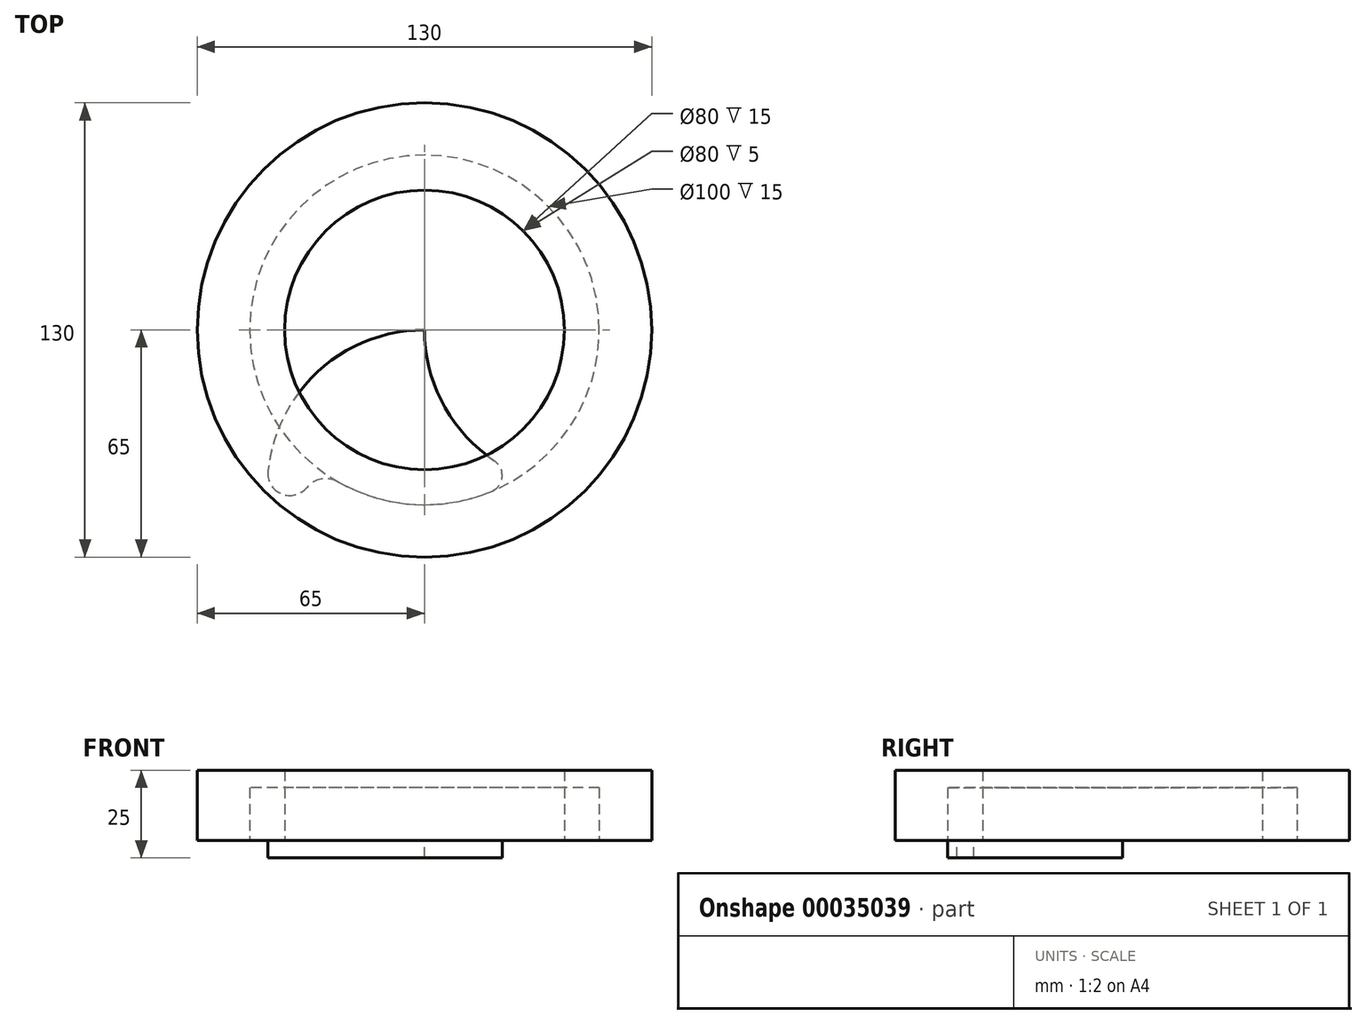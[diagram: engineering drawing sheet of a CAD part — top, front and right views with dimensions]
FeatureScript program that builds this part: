
annotation { "Feature Type Name" : "Feature", "Feature Type Description" : "" }
export const myFeature = defineFeature(function(context is Context, id is Id, definition is map)
    precondition{}
    {
        {
            var Q0;
            Q0=qCreatedBy(makeId("Top.planeOp"),FACE);
            var sketch = newSketch(context, id + "F0", { "sketchPlane" : qUnion([Q0])});
            skCircle(sketch, "E0", {"center": v(0, 0) * mm, "radius": 40 * mm});
            skCircle(sketch, "E1", {"center": v(0, 0) * mm, "radius": 50 * mm});
            skCircle(sketch, "E2", {"center": v(0, 0) * mm, "radius": 65 * mm});
            skLineSegment(sketch, "E3", {"start": v(50, 0) * mm, "end": v(40, 0) * mm});
            skPoint(sketch, "E4", {"position": v(45, 0) * mm});
            skCircle(sketch, "E5", {"center": v(45, 0) * mm, "radius": 45 * mm});
            skLineSegment(sketch, "E6", {"start": v(0, -40) * mm, "end": v(0, -50) * mm});
            skPoint(sketch, "E7", {"position": v(0, -45) * mm});
            skCircle(sketch, "E8", {"center": v(0, -45) * mm, "radius": 45 * mm});
            skCircle(sketch, "E9", {"center": v(-38.5, -41.07) * mm, "radius": 6.3 * mm});
            skArc(sketch, "E10", {"start": v(-24.73, -43.45) * mm, "mid": v(-29.5, -42.64) * mm, "end": v(-33.66, -45.08) * mm});
            skSolve(sketch);
        }
        {
            var Q0;
            {var subQ1=sQuery(id+"F0.wireOp",EDGE,"E1");var subQ5=sQuery(id+"F0.wireOp",EDGE,"E5");var subQ7=makeQuery(id+"F0.imprint","INTERSECT",VERTEX,{"disambiguationData":[OD(0.0)],"derivedFrom":[subQ1,subQ5]});Q0=makeQuery(id+"F0.imprint","IMPRINT",FACE,{"disambiguationData":[TD([[makeQuery(id+"F0.imprint","IMPRINT",EDGE,{"disambiguationData":[TD([[subQ7,-1.0]])],"derivedFrom":subQ1}),-1.0]])]});}
            var Q1;
            {var subQ5=sQuery(id+"F0.wireOp",EDGE,"E1");var subQ9=makeQuery(id+"F0.imprint","INTERSECT",VERTEX,{"derivedFrom":[subQ5,sQuery(id+"F0.wireOp",EDGE,"E6")]});Q1=makeQuery(id+"F0.imprint","IMPRINT",FACE,{"disambiguationData":[TD([[makeQuery(id+"F0.imprint","IMPRINT",EDGE,{"disambiguationData":[TD([[subQ9,1.0]])],"derivedFrom":subQ5}),-1.0]])]});}
            var Q2;
            {var subQ3=sQuery(id+"F0.wireOp",EDGE,"E1");var subQ11=makeQuery(id+"F0.imprint","INTERSECT",VERTEX,{"derivedFrom":[subQ3,sQuery(id+"F0.wireOp",EDGE,"E3")]});Q2=makeQuery(id+"F0.imprint","IMPRINT",FACE,{"disambiguationData":[TD([[makeQuery(id+"F0.imprint","IMPRINT",EDGE,{"disambiguationData":[TD([[subQ11,-1.0]])],"derivedFrom":subQ3}),-1.0]])]});}
            var Q3;
            {var subQ1=sQuery(id+"F0.wireOp",EDGE,"E5");var subQ3=sQuery(id+"F0.wireOp",EDGE,"E1");var subQ5=makeQuery(id+"F0.imprint","INTERSECT",VERTEX,{"disambiguationData":[OD(1.0)],"derivedFrom":[subQ3,subQ1]});Q3=makeQuery(id+"F0.imprint","IMPRINT",FACE,{"disambiguationData":[TD([[makeQuery(id+"F0.imprint","IMPRINT",EDGE,{"disambiguationData":[TD([[subQ5,-1.0]])],"derivedFrom":subQ3}),-1.0]])]});}
            var Q4;
            {var subQ0=sQuery(id+"F0.wireOp",EDGE,"94395ed1-b184-4d6a-bdb4-7635c48ce84e");var subQ3=sQuery(id+"F0.wireOp",EDGE,"E1");var subQ4=makeQuery(id+"F0.imprint","INTERSECT",VERTEX,{"derivedFrom":[subQ3,subQ0]});Q4=makeQuery(id+"F0.imprint","IMPRINT",FACE,{"disambiguationData":[TD([[makeQuery(id+"F0.imprint","IMPRINT",EDGE,{"disambiguationData":[TD([[subQ4,-1.0]])],"derivedFrom":subQ3}),-1.0]])]});}
            var Q5;
            {var subQ0=sQuery(id+"F0.wireOp",EDGE,"94395ed1-b184-4d6a-bdb4-7635c48ce84e");var subQ2=makeQuery(id+"F0.imprint","INTERSECT",VERTEX,{"derivedFrom":[sQuery(id+"F0.wireOp",EDGE,"E1"),subQ0]});Q5=makeQuery(id+"F0.imprint","IMPRINT",FACE,{"disambiguationData":[TD([[makeQuery(id+"F0.imprint","IMPRINT",EDGE,{"disambiguationData":[TD([[subQ2,1.0]])],"derivedFrom":subQ0}),1.0]])]});}
            var Q6;
            {var subQ0=sQuery(id+"F0.wireOp",EDGE,"E8");var subQ3=sQuery(id+"F0.wireOp",EDGE,"E2");var subQ4=makeQuery(id+"F0.imprint","INTERSECT",VERTEX,{"disambiguationData":[OD(1.0)],"derivedFrom":[subQ3,subQ0]});Q6=makeQuery(id+"F0.imprint","IMPRINT",FACE,{"disambiguationData":[TD([[makeQuery(id+"F0.imprint","IMPRINT",EDGE,{"disambiguationData":[TD([[subQ4,-1.0]])],"derivedFrom":subQ3}),1.0]])]});}
            var Q7;
            {var subQ3=sQuery(id+"F0.wireOp",EDGE,"E0");var subQ5=sQuery(id+"F0.wireOp",EDGE,"E5");var subQ7=makeQuery(id+"F0.imprint","INTERSECT",VERTEX,{"disambiguationData":[OD(0.0)],"derivedFrom":[subQ3,subQ5]});Q7=makeQuery(id+"F0.imprint","IMPRINT",FACE,{"disambiguationData":[TD([[makeQuery(id+"F0.imprint","IMPRINT",EDGE,{"disambiguationData":[TD([[subQ7,-1.0]])],"derivedFrom":subQ3}),-1.0]])]});}
            var Q8;
            {var subQ5=sQuery(id+"F0.wireOp",EDGE,"E3");Q8=makeQuery(id+"F0.imprint","IMPRINT",FACE,{"disambiguationData":[TD([[makeQuery(id+"F0.imprint","IMPRINT",EDGE,{"derivedFrom":subQ5}),-1.0]])]});}
            var Q9;
            {var subQ5=sQuery(id+"F0.wireOp",EDGE,"E3");Q9=makeQuery(id+"F0.imprint","IMPRINT",FACE,{"disambiguationData":[TD([[makeQuery(id+"F0.imprint","IMPRINT",EDGE,{"derivedFrom":subQ5}),1.0]])]});}
            var Q10;
            {var subQ3=sQuery(id+"F0.wireOp",EDGE,"E0");var subQ5=sQuery(id+"F0.wireOp",EDGE,"E5");var subQ7=makeQuery(id+"F0.imprint","INTERSECT",VERTEX,{"disambiguationData":[OD(1.0)],"derivedFrom":[subQ3,subQ5]});Q10=makeQuery(id+"F0.imprint","IMPRINT",FACE,{"disambiguationData":[TD([[makeQuery(id+"F0.imprint","IMPRINT",EDGE,{"disambiguationData":[TD([[subQ7,-1.0]])],"derivedFrom":subQ3}),-1.0]])]});}
            var Q11;
            {var subQ0=sQuery(id+"F0.wireOp",EDGE,"E6");Q11=makeQuery(id+"F0.imprint","IMPRINT",FACE,{"disambiguationData":[TD([[makeQuery(id+"F0.imprint","IMPRINT",EDGE,{"derivedFrom":subQ0}),1.0]])]});}
            var Q12;
            {var subQ5=sQuery(id+"F0.wireOp",EDGE,"E6");Q12=makeQuery(id+"F0.imprint","IMPRINT",FACE,{"disambiguationData":[TD([[makeQuery(id+"F0.imprint","IMPRINT",EDGE,{"derivedFrom":subQ5}),-1.0]])]});}
            var Q13;
            {var subQ1=sQuery(id+"F0.wireOp",EDGE,"E8");var subQ3=sQuery(id+"F0.wireOp",EDGE,"E1");var subQ5=makeQuery(id+"F0.imprint","INTERSECT",VERTEX,{"disambiguationData":[OD(0.0)],"derivedFrom":[subQ3,subQ1]});Q13=makeQuery(id+"F0.imprint","IMPRINT",FACE,{"disambiguationData":[TD([[makeQuery(id+"F0.imprint","IMPRINT",EDGE,{"disambiguationData":[TD([[subQ5,-1.0]])],"derivedFrom":subQ3}),-1.0]])]});}
            var Q14;
            {var subQ0=sQuery(id+"F0.wireOp",EDGE,"E9");var subQ2=makeQuery(id+"F0.imprint","INTERSECT",VERTEX,{"derivedFrom":[sQuery(id+"F0.wireOp",EDGE,"E1"),subQ0]});Q14=makeQuery(id+"F0.imprint","IMPRINT",FACE,{"disambiguationData":[TD([[makeQuery(id+"F0.imprint","IMPRINT",EDGE,{"disambiguationData":[TD([[subQ2,-1.0]])],"derivedFrom":subQ0}),1.0]])]});}
            var Q15;
            {var subQ0=sQuery(id+"F0.wireOp",EDGE,"E10");Q15=makeQuery(id+"F0.imprint","IMPRINT",FACE,{"disambiguationData":[TD([[makeQuery(id+"F0.imprint","IMPRINT",EDGE,{"derivedFrom":subQ0}),-1.0]])]});}
            extrude(context, id + "F1", {"entities" : qUnion([Q0, Q1, Q2, Q3, Q4, Q5, Q6, Q7, Q8, Q9, Q10, Q11, Q12, Q13, Q14, Q15]), "depth" : 20 * mm});
        }
        {
            var Q0;
            {var subQ5=sQuery(id+"F0.wireOp",EDGE,"E3");Q0=makeQuery(id+"F0.imprint","IMPRINT",FACE,{"disambiguationData":[TD([[makeQuery(id+"F0.imprint","IMPRINT",EDGE,{"derivedFrom":subQ5}),-1.0]])]});}
            var Q1;
            {var subQ5=sQuery(id+"F0.wireOp",EDGE,"E3");Q1=makeQuery(id+"F0.imprint","IMPRINT",FACE,{"disambiguationData":[TD([[makeQuery(id+"F0.imprint","IMPRINT",EDGE,{"derivedFrom":subQ5}),1.0]])]});}
            var Q2;
            {var subQ3=sQuery(id+"F0.wireOp",EDGE,"E0");var subQ5=sQuery(id+"F0.wireOp",EDGE,"E5");var subQ7=makeQuery(id+"F0.imprint","INTERSECT",VERTEX,{"disambiguationData":[OD(1.0)],"derivedFrom":[subQ3,subQ5]});Q2=makeQuery(id+"F0.imprint","IMPRINT",FACE,{"disambiguationData":[TD([[makeQuery(id+"F0.imprint","IMPRINT",EDGE,{"disambiguationData":[TD([[subQ7,-1.0]])],"derivedFrom":subQ3}),-1.0]])]});}
            var Q3;
            {var subQ0=sQuery(id+"F0.wireOp",EDGE,"E6");Q3=makeQuery(id+"F0.imprint","IMPRINT",FACE,{"disambiguationData":[TD([[makeQuery(id+"F0.imprint","IMPRINT",EDGE,{"derivedFrom":subQ0}),1.0]])]});}
            var Q4;
            {var subQ5=sQuery(id+"F0.wireOp",EDGE,"E6");Q4=makeQuery(id+"F0.imprint","IMPRINT",FACE,{"disambiguationData":[TD([[makeQuery(id+"F0.imprint","IMPRINT",EDGE,{"derivedFrom":subQ5}),-1.0]])]});}
            var Q5;
            {var subQ3=sQuery(id+"F0.wireOp",EDGE,"E0");var subQ5=sQuery(id+"F0.wireOp",EDGE,"E5");var subQ7=makeQuery(id+"F0.imprint","INTERSECT",VERTEX,{"disambiguationData":[OD(0.0)],"derivedFrom":[subQ3,subQ5]});Q5=makeQuery(id+"F0.imprint","IMPRINT",FACE,{"disambiguationData":[TD([[makeQuery(id+"F0.imprint","IMPRINT",EDGE,{"disambiguationData":[TD([[subQ7,-1.0]])],"derivedFrom":subQ3}),-1.0]])]});}
            extrude(context, id + "F2", {"entities" : qUnion([Q0, Q1, Q2, Q3, Q4, Q5]), "operationType" : NewBodyOperationType.REMOVE, "depth" : 15 * mm});
        }
        {
            var Q0;
            {var subQ5=sQuery(id+"F0.wireOp",EDGE,"E6");Q0=makeQuery(id+"F0.imprint","IMPRINT",FACE,{"disambiguationData":[TD([[makeQuery(id+"F0.imprint","IMPRINT",EDGE,{"derivedFrom":subQ5}),-1.0]])]});}
            var Q1;
            {var subQ0=sQuery(id+"F0.wireOp",EDGE,"E6");Q1=makeQuery(id+"F0.imprint","IMPRINT",FACE,{"disambiguationData":[TD([[makeQuery(id+"F0.imprint","IMPRINT",EDGE,{"derivedFrom":subQ0}),1.0]])]});}
            var Q2;
            {var subQ3=sQuery(id+"F0.wireOp",EDGE,"E0");var subQ5=sQuery(id+"F0.wireOp",EDGE,"E5");var subQ7=makeQuery(id+"F0.imprint","INTERSECT",VERTEX,{"disambiguationData":[OD(1.0)],"derivedFrom":[subQ3,subQ5]});Q2=makeQuery(id+"F0.imprint","IMPRINT",FACE,{"disambiguationData":[TD([[makeQuery(id+"F0.imprint","IMPRINT",EDGE,{"disambiguationData":[TD([[subQ7,-1.0]])],"derivedFrom":subQ3}),-1.0]])]});}
            var Q3;
            {var subQ5=sQuery(id+"F0.wireOp",EDGE,"E3");Q3=makeQuery(id+"F0.imprint","IMPRINT",FACE,{"disambiguationData":[TD([[makeQuery(id+"F0.imprint","IMPRINT",EDGE,{"derivedFrom":subQ5}),1.0]])]});}
            var Q4;
            {var subQ5=sQuery(id+"F0.wireOp",EDGE,"E3");Q4=makeQuery(id+"F0.imprint","IMPRINT",FACE,{"disambiguationData":[TD([[makeQuery(id+"F0.imprint","IMPRINT",EDGE,{"derivedFrom":subQ5}),-1.0]])]});}
            var Q5;
            {var subQ3=sQuery(id+"F0.wireOp",EDGE,"E0");var subQ5=sQuery(id+"F0.wireOp",EDGE,"E5");var subQ7=makeQuery(id+"F0.imprint","INTERSECT",VERTEX,{"disambiguationData":[OD(0.0)],"derivedFrom":[subQ3,subQ5]});Q5=makeQuery(id+"F0.imprint","IMPRINT",FACE,{"disambiguationData":[TD([[makeQuery(id+"F0.imprint","IMPRINT",EDGE,{"disambiguationData":[TD([[subQ7,-1.0]])],"derivedFrom":subQ3}),-1.0]])]});}
            extrude(context, id + "F3", {"entities" : qUnion([Q0, Q1, Q2, Q3, Q4, Q5]), "depth" : 15 * mm});
        }
        {
            var Q0;
            {var subQ3=sQuery(id+"F0.wireOp",EDGE,"E0");var subQ6=makeQuery(id+"F0.imprint","INTERSECT",VERTEX,{"derivedFrom":[subQ3,sQuery(id+"F0.wireOp",EDGE,"E6")]});Q0=makeQuery(id+"F0.imprint","IMPRINT",FACE,{"disambiguationData":[TD([[makeQuery(id+"F0.imprint","IMPRINT",EDGE,{"disambiguationData":[TD([[subQ6,1.0]])],"derivedFrom":subQ3}),1.0]])]});}
            var Q1;
            {var subQ0=sQuery(id+"F0.wireOp",EDGE,"E6");Q1=makeQuery(id+"F0.imprint","IMPRINT",FACE,{"disambiguationData":[TD([[makeQuery(id+"F0.imprint","IMPRINT",EDGE,{"derivedFrom":subQ0}),1.0]])]});}
            var Q2;
            {var subQ5=sQuery(id+"F0.wireOp",EDGE,"E6");Q2=makeQuery(id+"F0.imprint","IMPRINT",FACE,{"disambiguationData":[TD([[makeQuery(id+"F0.imprint","IMPRINT",EDGE,{"derivedFrom":subQ5}),-1.0]])]});}
            var Q3;
            {var subQ1=sQuery(id+"F0.wireOp",EDGE,"E8");var subQ3=sQuery(id+"F0.wireOp",EDGE,"E1");var subQ5=makeQuery(id+"F0.imprint","INTERSECT",VERTEX,{"disambiguationData":[OD(0.0)],"derivedFrom":[subQ3,subQ1]});Q3=makeQuery(id+"F0.imprint","IMPRINT",FACE,{"disambiguationData":[TD([[makeQuery(id+"F0.imprint","IMPRINT",EDGE,{"disambiguationData":[TD([[subQ5,-1.0]])],"derivedFrom":subQ3}),-1.0]])]});}
            var Q4;
            {var subQ0=sQuery(id+"F0.wireOp",EDGE,"E9");var subQ2=makeQuery(id+"F0.imprint","INTERSECT",VERTEX,{"derivedFrom":[sQuery(id+"F0.wireOp",EDGE,"E1"),subQ0]});Q4=makeQuery(id+"F0.imprint","IMPRINT",FACE,{"disambiguationData":[TD([[makeQuery(id+"F0.imprint","IMPRINT",EDGE,{"disambiguationData":[TD([[subQ2,-1.0]])],"derivedFrom":subQ0}),1.0]])]});}
            var Q5;
            {var subQ0=sQuery(id+"F0.wireOp",EDGE,"E10");Q5=makeQuery(id+"F0.imprint","IMPRINT",FACE,{"disambiguationData":[TD([[makeQuery(id+"F0.imprint","IMPRINT",EDGE,{"derivedFrom":subQ0}),-1.0]])]});}
            extrude(context, id + "F4", {"entities" : qUnion([Q0, Q1, Q2, Q3, Q4, Q5]), "oppositeDirection" : true, "depth" : 5 * mm});
        }
        {
            var Q0;
            Q0=makeQuery(id+"F4.opExtrude","SWEPT_EDGE",EDGE,{"disambiguationData":[OSD([sQuery(id+"F0.wireOp",EDGE,"E1"),sQuery(id+"F0.wireOp",EDGE,"E5")])]});
            fillet(context, id + "F5", {"entities" : qUnion([Q0]), "radius" : 5 * mm, "tangentPropagation" : true, "allowEdgeOverflow" : false});
        }
    });
